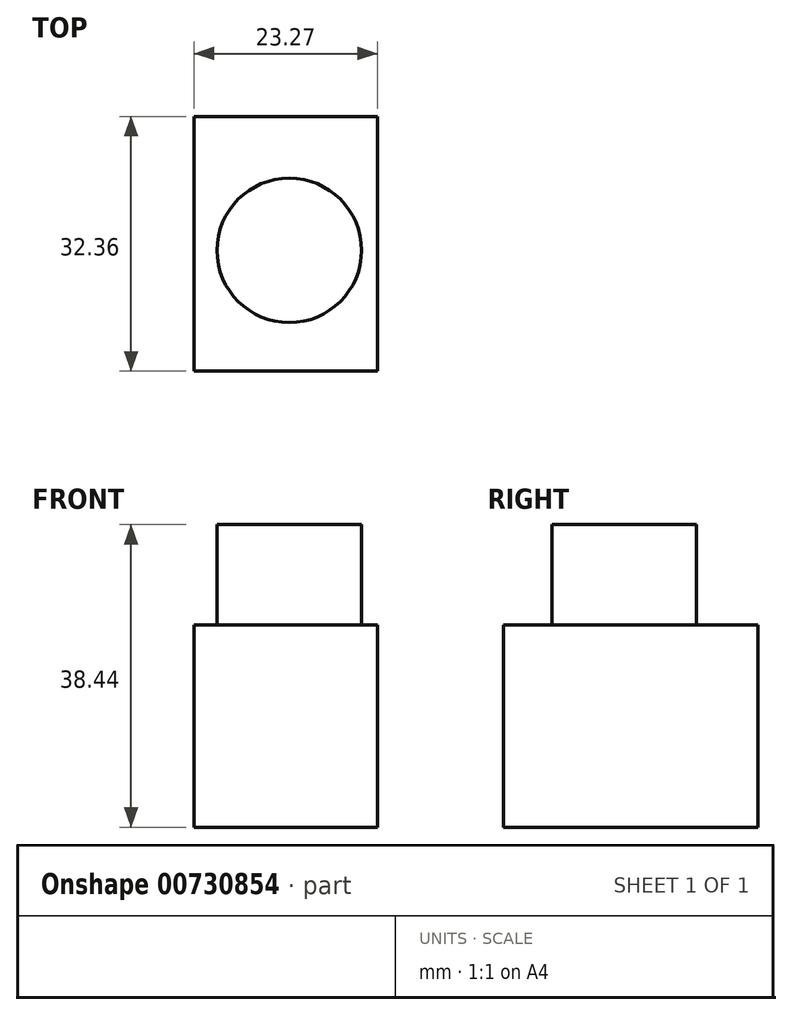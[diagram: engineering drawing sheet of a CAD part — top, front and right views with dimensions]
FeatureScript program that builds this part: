
annotation { "Feature Type Name" : "Feature", "Feature Type Description" : "" }
export const myFeature = defineFeature(function(context is Context, id is Id, definition is map)
    precondition{}
    {
        {
            var Q0;
            Q0=qCreatedBy(makeId("Front.planeOp"),FACE);
            var sketch = newSketch(context, id + "F0", { "sketchPlane" : qUnion([Q0])});
            skLineSegment(sketch, "E0.bottom", {"start": v(21.8, 0) * mm, "end": v(45.07, 0) * mm});
            skLineSegment(sketch, "E0.top", {"start": v(21.8, -25.68) * mm, "end": v(45.07, -25.68) * mm});
            skLineSegment(sketch, "E0.left", {"start": v(21.8, 0) * mm, "end": v(21.8, -25.68) * mm});
            skLineSegment(sketch, "E0.right", {"start": v(45.07, 0) * mm, "end": v(45.07, -25.68) * mm});
            skSolve(sketch);
        }
        {
            var Q0;
            Q0=makeQuery(id+"F0.imprint","IMPRINT",FACE,{"disambiguationData":[TD([[makeQuery(id+"F0.imprint","IMPRINT",EDGE,{"derivedFrom":sQuery(id+"F0.wireOp",EDGE,"E0.bottom")}),-1.0]])]});
            extrude(context, id + "F1", {"entities" : qUnion([Q0]), "depth" : 32.36 * mm, "offsetDistance" : 25.4 * mm});
        }
        {
            var Q0;
            Q0=makeQuery(id+"F1.opExtrude","SWEPT_FACE",FACE,{"disambiguationData":[OSD([sQuery(id+"F0.wireOp",EDGE,"E0.bottom")])]});
            var sketch = newSketch(context, id + "F2", { "sketchPlane" : qUnion([Q0])});
            skCircle(sketch, "E1", {"center": v(33.89, -17.03) * mm, "radius": 9.18 * mm});
            skSolve(sketch);
        }
        {
            var Q0;
            Q0=makeQuery(id+"F2.imprint","IMPRINT",FACE,{"disambiguationData":[TD([[makeQuery(id+"F2.imprint","IMPRINT",EDGE,{"derivedFrom":sQuery(id+"F2.wireOp",EDGE,"E1")}),1.0]])]});
            extrude(context, id + "F3", {"entities" : qUnion([Q0]), "operationType" : NewBodyOperationType.ADD, "depth" : 12.76 * mm, "offsetDistance" : 25.4 * mm});
        }
    });
